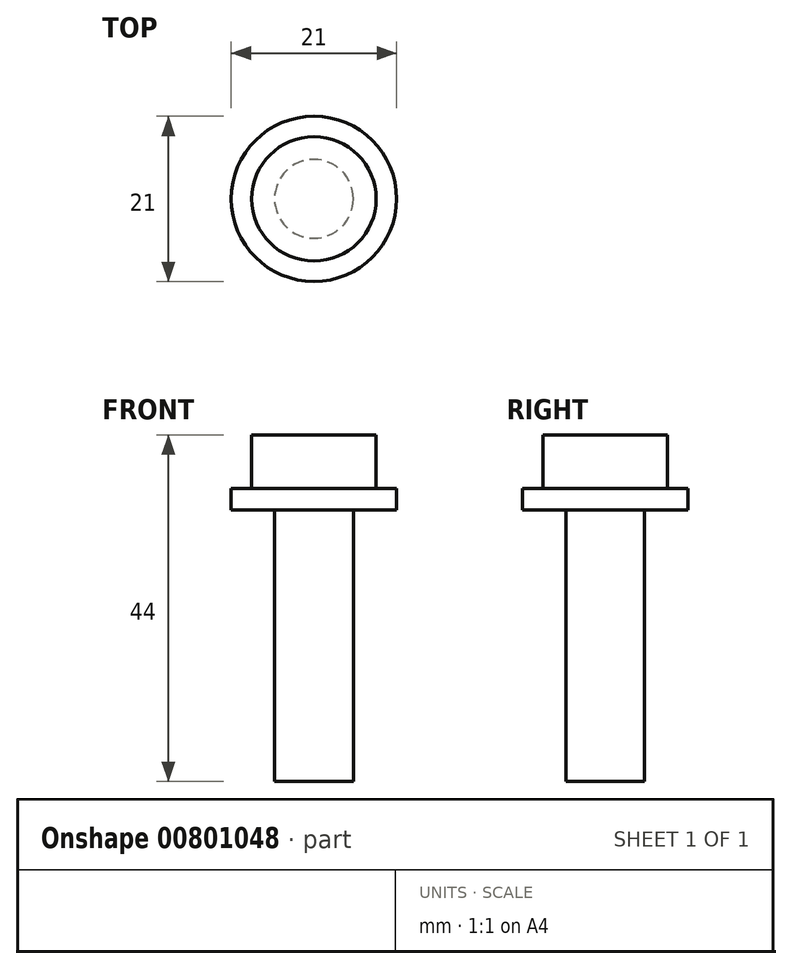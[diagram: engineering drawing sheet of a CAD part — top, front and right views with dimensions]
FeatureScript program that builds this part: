
annotation { "Feature Type Name" : "Feature", "Feature Type Description" : "" }
export const myFeature = defineFeature(function(context is Context, id is Id, definition is map)
    precondition{}
    {
        {
            var Q0;
            Q0=qCreatedBy(makeId("Front.planeOp"),FACE);
            var sketch = newSketch(context, id + "F0", { "sketchPlane" : qUnion([Q0])});
            skLineSegment(sketch, "E0", {"start": v(0, 0) * mm, "end": v(0, -44) * mm});
            skLineSegment(sketch, "E1", {"start": v(0, -44) * mm, "end": v(5, -44) * mm});
            skLineSegment(sketch, "E2", {"start": v(5, -44) * mm, "end": v(5, -9.5) * mm});
            skLineSegment(sketch, "E3", {"start": v(5, -9.5) * mm, "end": v(10.5, -9.5) * mm});
            skLineSegment(sketch, "E4", {"start": v(10.5, -9.5) * mm, "end": v(10.5, -6.8) * mm});
            skLineSegment(sketch, "E5", {"start": v(10.5, -6.8) * mm, "end": v(7.9, -6.8) * mm});
            skLineSegment(sketch, "E6", {"start": v(7.9, -6.8) * mm, "end": v(7.9, 0) * mm});
            skLineSegment(sketch, "E7", {"start": v(7.9, 0) * mm, "end": v(0, 0) * mm});
            skSolve(sketch);
        }
        {
            var Q0;
            Q0=makeQuery(id+"F0.imprint","IMPRINT",FACE,{"disambiguationData":[TD([[makeQuery(id+"F0.imprint","IMPRINT",EDGE,{"derivedFrom":sQuery(id+"F0.wireOp",EDGE,"E0")}),1.0]])]});
            var Q1;
            Q1=sQuery(id+"F0.wireOp",EDGE,"E0");
            revolve(context, id + "F1", {"surfaceOperationType" : NewSurfaceOperationType.NEW, "entities" : qUnion([Q0]), "axis" : qUnion([Q1]), "revolveType" : RevolveType.FULL});
        }
    });
